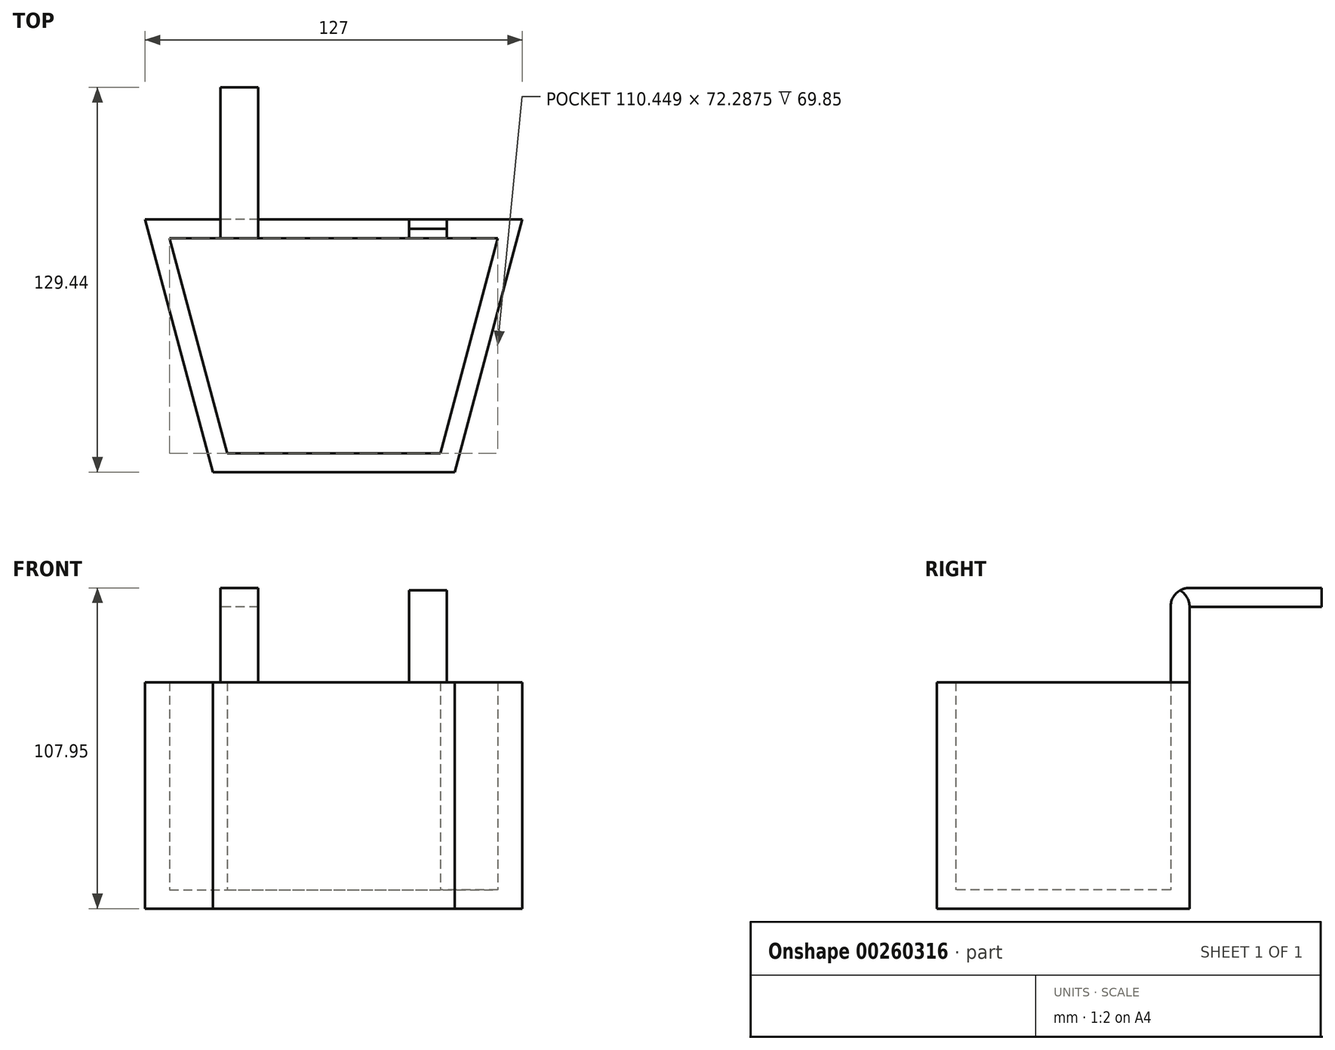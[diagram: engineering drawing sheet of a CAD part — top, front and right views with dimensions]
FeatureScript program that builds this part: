
annotation { "Feature Type Name" : "Feature", "Feature Type Description" : "" }
export const myFeature = defineFeature(function(context is Context, id is Id, definition is map)
    precondition{}
    {
        {
            var Q0;
            Q0=qCreatedBy(makeId("Top.planeOp"),FACE);
            var sketch = newSketch(context, id + "F0", { "sketchPlane" : qUnion([Q0])});
            skLineSegment(sketch, "E0", {"start": v(-168.54, 78.87) * mm, "end": v(-295.54, 78.87) * mm});
            skLineSegment(sketch, "E1", {"start": v(-168.54, 78.87) * mm, "end": v(-191.3, -6.12) * mm});
            skLineSegment(sketch, "E2", {"start": v(-295.54, 78.87) * mm, "end": v(-272.76, -6.12) * mm});
            skLineSegment(sketch, "E3", {"start": v(-272.76, -6.12) * mm, "end": v(-191.3, -6.12) * mm});
            skLineSegment(sketch, "E4", {"start": v(-287.26, 72.52) * mm, "end": v(-176.81, 72.52) * mm});
            skLineSegment(sketch, "E5", {"start": v(-287.26, 72.52) * mm, "end": v(-267.9, 0.23) * mm});
            skLineSegment(sketch, "E6", {"start": v(-176.81, 72.52) * mm, "end": v(-196.18, 0.23) * mm});
            skLineSegment(sketch, "E7", {"start": v(-267.9, 0.23) * mm, "end": v(-196.18, 0.23) * mm});
            skSolve(sketch);
        }
        {
            var Q0;
            Q0 = qSketchRegion(id + "F0", true);
            extrude(context, id + "F1", {"entities" : qUnion([Q0]), "depth" : 76.2 * mm});
        }
        {
            var Q0;
            Q0=makeQuery(id+"F0.imprint","IMPRINT",FACE,{"disambiguationData":[TD([[makeQuery(id+"F0.imprint","IMPRINT",EDGE,{"derivedFrom":sQuery(id+"F0.wireOp",EDGE,"E4")}),-1.0]])]});
            extrude(context, id + "F2", {"entities" : qUnion([Q0]), "operationType" : NewBodyOperationType.ADD, "depth" : 6.35 * mm});
        }
        {
            var Q0;
            Q0=makeQuery(id+"F1.opExtrude","SWEPT_FACE",FACE,{"disambiguationData":[OSD([sQuery(id+"F0.wireOp",EDGE,"E0")])]});
            var sketch = newSketch(context, id + "F3", { "sketchPlane" : qUnion([Q0])});
            skLineSegment(sketch, "E8.bottom", {"start": v(193.94, 76.2) * mm, "end": v(206.64, 76.2) * mm});
            skLineSegment(sketch, "E8.top", {"start": v(193.94, 101.6) * mm, "end": v(206.64, 101.6) * mm});
            skLineSegment(sketch, "E8.left", {"start": v(193.94, 76.2) * mm, "end": v(193.94, 101.6) * mm});
            skLineSegment(sketch, "E8.right", {"start": v(206.64, 76.2) * mm, "end": v(206.64, 101.6) * mm});
            skLineSegment(sketch, "E9.bottom", {"start": v(257.44, 76.2) * mm, "end": v(270.14, 76.2) * mm});
            skLineSegment(sketch, "E9.top", {"start": v(257.44, 101.6) * mm, "end": v(270.14, 101.6) * mm});
            skLineSegment(sketch, "E9.left", {"start": v(257.44, 76.2) * mm, "end": v(257.44, 101.6) * mm});
            skLineSegment(sketch, "E9.right", {"start": v(270.14, 76.2) * mm, "end": v(270.14, 101.6) * mm});
            skSolve(sketch);
        }
        {
            var Q0;
            Q0=makeQuery(id+"F3.imprint","IMPRINT",FACE,{"disambiguationData":[TD([[makeQuery(id+"F3.imprint","IMPRINT",EDGE,{"derivedFrom":sQuery(id+"F3.wireOp",EDGE,"E8.bottom")}),1.0]])]});
            var Q1;
            Q1=makeQuery(id+"F3.imprint","IMPRINT",FACE,{"disambiguationData":[TD([[makeQuery(id+"F3.imprint","IMPRINT",EDGE,{"derivedFrom":sQuery(id+"F3.wireOp",EDGE,"E9.bottom")}),1.0]])]});
            extrude(context, id + "F4", {"entities" : qUnion([Q0, Q1]), "operationType" : NewBodyOperationType.ADD, "oppositeDirection" : true, "depth" : 6.35 * mm});
        }
        {
            var Q0;
            Q0=makeQuery(id+"F4.opExtrude","SWEPT_FACE",FACE,{"disambiguationData":[OSD([sQuery(id+"F3.wireOp",EDGE,"E8.top")])]});
            var sketch = newSketch(context, id + "F5", { "sketchPlane" : qUnion([Q0])});
            skLineSegment(sketch, "E10.bottom", {"start": v(-206.64, 72.52) * mm, "end": v(-206.64, 72.52) * mm});
            skLineSegment(sketch, "E10.top", {"start": v(-206.64, 123.32) * mm, "end": v(-206.64, 123.32) * mm});
            skLineSegment(sketch, "E10.left", {"start": v(-206.64, 72.52) * mm, "end": v(-206.64, 123.32) * mm});
            skLineSegment(sketch, "E10.right", {"start": v(-206.64, 72.52) * mm, "end": v(-206.64, 123.32) * mm});
            skLineSegment(sketch, "E11.bottom", {"start": v(-193.94, 72.52) * mm, "end": v(-193.94, 72.52) * mm});
            skLineSegment(sketch, "E11.top", {"start": v(-193.94, 123.32) * mm, "end": v(-193.94, 123.32) * mm});
            skLineSegment(sketch, "E11.left", {"start": v(-193.94, 72.52) * mm, "end": v(-193.94, 123.32) * mm});
            skLineSegment(sketch, "E11.right", {"start": v(-193.94, 72.52) * mm, "end": v(-193.94, 123.32) * mm});
            skLineSegment(sketch, "E12.bottom", {"start": v(-206.64, 123.32) * mm, "end": v(-193.94, 123.32) * mm});
            skLineSegment(sketch, "E12.top", {"start": v(-206.64, 123.32) * mm, "end": v(-193.94, 123.32) * mm});
            skSolve(sketch);
        }
        {
            var Q0;
            {var subQ1=sQuery(id+"F3.wireOp",EDGE,"E8.top");var subQ2=makeQuery(id+"F4.opExtrude","CAP_EDGE",EDGE,{"disambiguationData":[OSD([subQ1])],"isStart":true});Q0=makeQuery(id+"F5.imprint","IMPRINT",FACE,{"disambiguationData":[TD([[makeQuery(id+"F5.imprint","IMPRINT",EDGE,{"derivedFrom":subQ2}),1.0]])]});}
            var Q1;
            {var subQ2=sQuery(id+"F5.wireOp",EDGE,"E12.top");Q1=makeQuery(id+"F5.imprint","IMPRINT",FACE,{"disambiguationData":[TD([[makeQuery(id+"F5.imprint","IMPRINT",EDGE,{"derivedFrom":subQ2}),-1.0]])]});}
            extrude(context, id + "F6", {"entities" : qUnion([Q0, Q1]), "operationType" : NewBodyOperationType.ADD, "depth" : 6.35 * mm});
        }
        {
            var Q0;
            Q0=makeQuery(id+"F4.opExtrude","SWEPT_FACE",FACE,{"disambiguationData":[OSD([sQuery(id+"F3.wireOp",EDGE,"E9.top")])]});
            var sketch = newSketch(context, id + "F7", { "sketchPlane" : qUnion([Q0])});
            skLineSegment(sketch, "E13", {"start": v(-270.14, 72.52) * mm, "end": v(-270.14, 123.32) * mm});
            skLineSegment(sketch, "E14", {"start": v(-270.14, 123.32) * mm, "end": v(-257.44, 123.32) * mm});
            skLineSegment(sketch, "E15", {"start": v(-257.44, 123.32) * mm, "end": v(-257.44, 72.52) * mm});
            skSolve(sketch);
        }
        {
            var Q0;
            {var subQ2=sQuery(id+"F7.wireOp",EDGE,"E14");Q0=makeQuery(id+"F7.imprint","IMPRINT",FACE,{"disambiguationData":[TD([[makeQuery(id+"F7.imprint","IMPRINT",EDGE,{"derivedFrom":subQ2}),-1.0]])]});}
            var Q1;
            {var subQ1=sQuery(id+"F3.wireOp",EDGE,"E9.top");var subQ2=makeQuery(id+"F4.opExtrude","CAP_EDGE",EDGE,{"disambiguationData":[OSD([subQ1])],"isStart":true});Q1=makeQuery(id+"F7.imprint","IMPRINT",FACE,{"disambiguationData":[TD([[makeQuery(id+"F7.imprint","IMPRINT",EDGE,{"derivedFrom":subQ2}),1.0]])]});}
            extrude(context, id + "F8", {"entities" : qUnion([Q0, Q1]), "operationType" : NewBodyOperationType.ADD, "depth" : 6.35 * mm});
        }
        {
            var Q0;
            Q0=makeQuery(id+"F6.opExtrude","CAP_EDGE",EDGE,{"disambiguationData":[OSD([sQuery(id+"F3.wireOp",EDGE,"E8.top")])],"isStart":false});
            fillet(context, id + "F9", {"entities" : qUnion([Q0]), "radius" : 6.35 * mm, "tangentPropagation" : true, "allowEdgeOverflow" : false});
        }
        {
            var Q0;
            Q0=makeQuery(id+"F8.opExtrude","CAP_EDGE",EDGE,{"disambiguationData":[OSD([sQuery(id+"F3.wireOp",EDGE,"E9.top")])],"isStart":false});
            fillet(context, id + "F10", {"entities" : qUnion([Q0]), "radius" : 6.35 * mm, "tangentPropagation" : true, "allowEdgeOverflow" : false});
        }
    });
